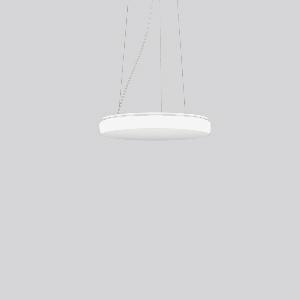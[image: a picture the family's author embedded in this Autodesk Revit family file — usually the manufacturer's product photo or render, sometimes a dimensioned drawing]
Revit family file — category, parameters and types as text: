
# Revit family: flat_polymero_kreis_slim_312090_002_1_733c
name_source: partatom
category: Lighting Fixtures
units: mm (PartAtom-declared; Revit-internal decimal feet)

## family parameters
Cut with Voids When Loaded = No
Host = Face
Light Source = No
Part Type = Normal
Room Calculation Point = No
Round Connector Dimension = Use Diameter
Shared = No

## types (1)
- FLAT POLYMERO KREIS SLIM (1 x LED Modul 830, 1900 lm, 3000)
    Apparent Load = 19 VA
    CIE Flux Codes = 43 74 93 88 100
    Color Rendering = 80
    Color Temperature = 3000
    Default Elevation = 1800 mm
    Description = Series: FLAT POLYMERO KREIS SLIM
Decorative round LED pendant luminaire. Base and canopy: metal, powder-coated, white. Canopy Ø 205 mm, h 35 mm. Diffuser made of non-yellowing plastic (PMMA), opal. Diffuser fastening: patented push system. Homogeneous and smooth light distribution. Suitable for pendant. 3-point steel cable suspension, steplessly adjustable. Special lengths available on request. 
Colour: white
Diameter: 460 mm
Height: 68 mm
Suspension length: 200-1300 mm
Lamp: LED
Socket: without socket
Colour temperature: 3000K
Colour rendering index (CRI): 80
System power: 19 W
Rated luminous flux: 1900 lm
Luminous efficiency: 100 lm/W
Control gear: AC Strom, dim.Ph.an-/abschnitt
Protection class: I
Type of protection: IP 40
    Height = 68 mm
    Lamp = 1 x LED Modul 830
    Lamp Light Flux = 1900 lm
    Lamp count = 1
    Length = 460 mm
    Lifetime = 50000 h
    Luminous efficacy = 100 lm/W
    Manufacturer = RZB
    ModVariant = No
    Model = 312090.002.1
    Mounting Place = Ceiling
    Mounting Type = Pendant
    Number of Poles = 1
    OnlyDefault = Yes
    Power Factor = 1
    Product Name = FLAT POLYMERO KREIS SLIM
    Product group = Pendant luminaires
    ProductGroupID = 902
    Protection Class = Protection class I
    Protection Degree = IP 40
    RLX_Detail_Level = 1
    RLX_Emergency_Light_Flux = 0 lm
    RLX_Emergency_Type = 0
    RLX_Emergency_Type_DB = No
    RlxData = <blob elided: 57993 chars, md5=139bd05b>
    Socket = socket
    Standby Power = 0 W
    System Light Flux = 1900 lm
    System Power = 19 W
    Type Comments = Product without accessories
    Type Image = 312090.002.jpg
    URL = http://relux.com
    VarID = ---
    Voltage = 230 V
    Voltage Range = 220-240 V
    Weight = 0.00 kg
    Width = 0 mm  [stored 0 ft]

note: [stored X ft] marks values corroborated as IEEE doubles in the binary element streams (Revit-internal decimal feet)

## geometry (parser evidence)
native form markers: Blend x4, Sweep x11
no freeform markers — native parametric forms only
